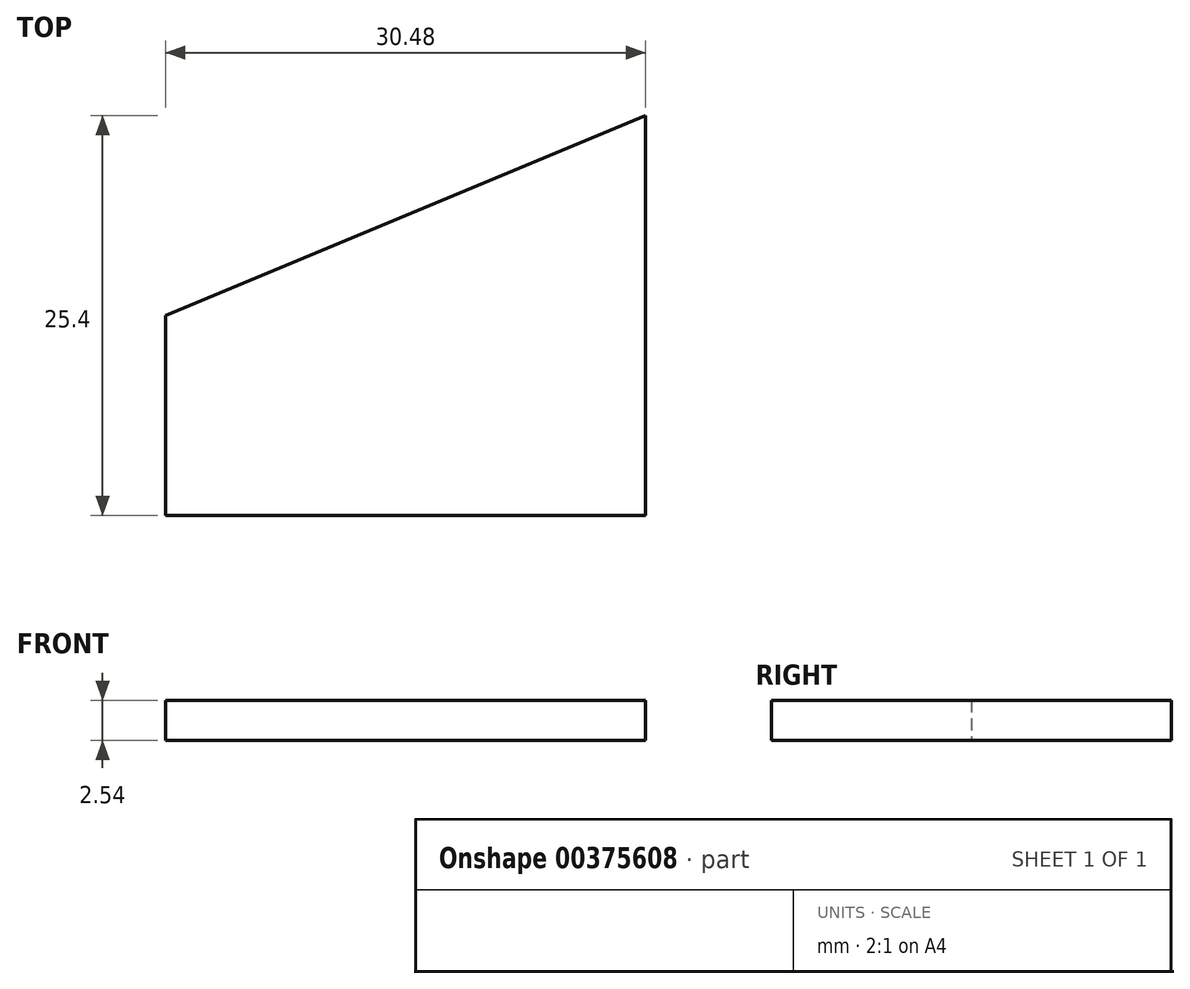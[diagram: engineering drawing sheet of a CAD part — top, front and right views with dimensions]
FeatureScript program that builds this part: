
annotation { "Feature Type Name" : "Feature", "Feature Type Description" : "" }
export const myFeature = defineFeature(function(context is Context, id is Id, definition is map)
    precondition{}
    {
        {
            var Q0;
            Q0=qCreatedBy(makeId("Top.planeOp"),FACE);
            var sketch = newSketch(context, id + "F0", { "sketchPlane" : qUnion([Q0])});
            skLineSegment(sketch, "E0", {"start": v(6.83, 6.95) * mm, "end": v(6.83, -18.45) * mm});
            skLineSegment(sketch, "E1", {"start": v(6.83, -18.45) * mm, "end": v(-23.65, -18.45) * mm});
            skLineSegment(sketch, "E2", {"start": v(-23.65, -18.45) * mm, "end": v(-23.65, -5.75) * mm});
            skLineSegment(sketch, "E3", {"start": v(-23.65, -5.75) * mm, "end": v(6.83, 6.95) * mm});
            skSolve(sketch);
        }
        {
            var Q0;
            Q0=makeQuery(id+"F0.imprint","IMPRINT",FACE,{"disambiguationData":[TD([[makeQuery(id+"F0.imprint","IMPRINT",EDGE,{"derivedFrom":sQuery(id+"F0.wireOp",EDGE,"E0")}),-1.0]])]});
            extrude(context, id + "F1", {"entities" : qUnion([Q0]), "depth" : 2.54 * mm});
        }
    });
